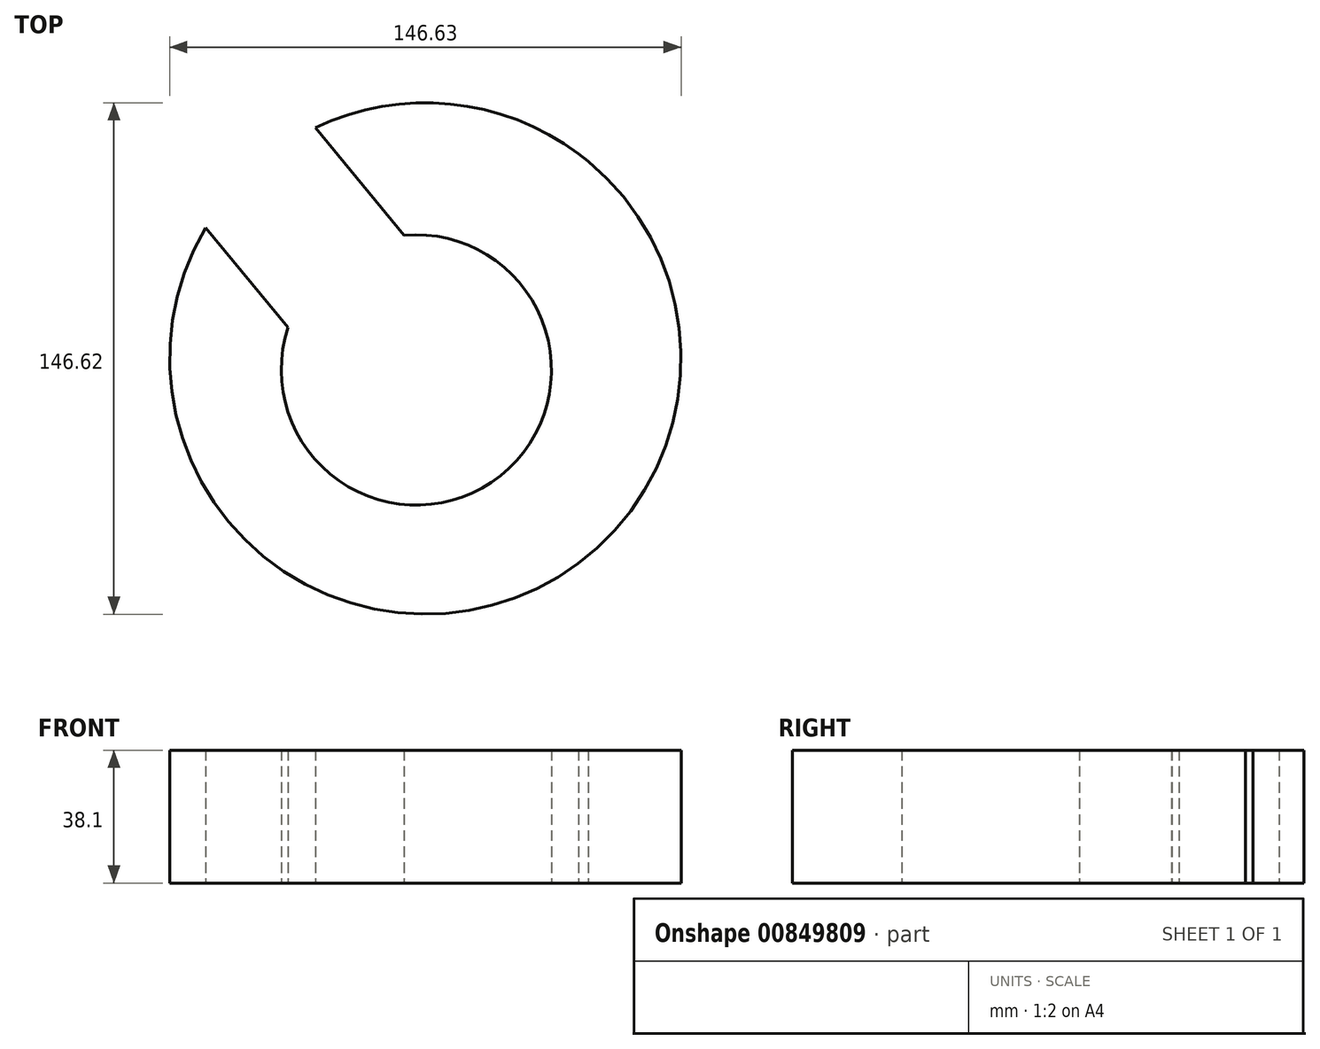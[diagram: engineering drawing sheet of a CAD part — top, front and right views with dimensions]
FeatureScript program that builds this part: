
annotation { "Feature Type Name" : "Feature", "Feature Type Description" : "" }
export const myFeature = defineFeature(function(context is Context, id is Id, definition is map)
    precondition{}
    {
        {
            var Q0;
            Q0=qCreatedBy(makeId("Top.planeOp"),FACE);
            var sketch = newSketch(context, id + "F0", { "sketchPlane" : qUnion([Q0])});
            skArc(sketch, "E0", {"start": v(-56.95, 15.12) * mm, "mid": v(55.48, -76.5) * mm, "end": v(-25.5, 43.82) * mm});
            skLineSegment(sketch, "E1", {"start": v(-25.5, 43.82) * mm, "end": v(0, 12.98) * mm});
            skLineSegment(sketch, "E2", {"start": v(49.92, 36.4) * mm, "end": v(52.77, 34.16) * mm});
            skLineSegment(sketch, "E3", {"start": v(-56.95, 15.12) * mm, "end": v(-33.32, -13.48) * mm});
            skArc(sketch, "E4", {"start": v(-33.32, -13.48) * mm, "mid": v(27.57, -55.95) * mm, "end": v(0, 12.98) * mm});
            skSolve(sketch);
        }
        {
            var Q0;
            {var subQ1=sQuery(id+"F0.wireOp",EDGE,"E1");Q0=makeQuery(id+"F0.imprint","IMPRINT",FACE,{"disambiguationData":[TD([[makeQuery(id+"F0.imprint","IMPRINT",EDGE,{"derivedFrom":subQ1}),1.0]])]});}
            extrude(context, id + "F1", {"entities" : qUnion([Q0]), "depth" : 38.1 * mm, "offsetDistance" : 25.4 * mm});
        }
    });
